# Revit family: Sanitary_Accessories_Johnson-Suisse_Cube_Single_Towel_Rail_60cm
name_source: partatom
category: Plumbing Fixtures
revit_build: Autodesk Revit 2015 (Build: 20140606_1530(x64)
units: mm (PartAtom-declared; Revit-internal decimal feet)

## types (1)
- Cube Single Towel Rail 60cm
    BIMobject category = Accessories
    Brand url = http://www.johnsonsuisse.com.au
    Design country = Spain
    EAN code = https://9325304004532
    Edition number = 1
    IFC Classification = Furnishing Element
    Manufacturer country = China
    Manufacturer name = Johnson Suisse
    Material main = Metal
    Material secondary = Chrome
    NBS Reference Code = 35-75-90
    NBS Reference Description = Towel Rails
    Nominal height = 45 mm  [stored 0.147638 ft]
    Nominal width = 600 mm  [stored 1.9685 ft]
    OmniClass Code = 23-31 25 25
    OmniClass Description = Towel Bars
    Product Guid = df7b0822-6060-49ca-893b-f3e301713f91
    Product SKU = GDC160165
    Product data url = https://bimobject.com
    Product family = Cube
    Product group = Accessories
    Product url = https://johnsonsuisse.com.au
    QR code = http://bimobject.com
    Technical description = https://johnsonsuisse.com.au
    Type = cube_single_towel_rail_60cm : Default
    UNSPSC Code = 301815
    Uniclass 1.4 Code = L8245
    Uniclass 1.4 Description = Towel rails
    Uniclass 2.0 Code = PR-35-75-90
    Uniclass 2.0 Description = Towel Rails
    Uniclass 2015 Code = Pr_40_20_76_90
    Uniclass 2015 Name = Towel rails
    Weight Net (Kg) = 0.455

note: [stored X ft] marks values corroborated as IEEE doubles in the binary element streams (Revit-internal decimal feet)

## geometry (parser evidence)
native form markers: Sweep x6
no freeform markers — native parametric forms only
